# Revit family: Storage_Rack-Honeywell-Cabinet_Housing-584910(11)(13)
name_source: partatom
category: Furniture
revit_build: Autodesk Revit 2017 (Build: 20160225_1515(x64)
units: mm (PartAtom-declared; Revit-internal decimal feet)

## family parameters
Cut with Voids When Loaded = No
Host = Face
OmniClass Number = 23.40.20.27.17
OmniClass Title = Racking
Room Calculation Point = No
Shared = No

## types (3) — shared parameters
Finish = Metal - Honeywell - Stainless Steel - White
Manufacturer = Honeywell International
Manufacturer Fax Number = 02131/40615-606
Product Documentation Link = https://www.esser-systems.com
Product Page URL = https://www.esser-systems.com
URL = www.esser-systems.com
Version = 2017 - v1.0a
zero-valued in all types: Default Elevation

## per-type parameters (varying)
| type | C Door | Constraints | Depth | Description | Height | Model | Product Name | Upright | VARIODYN | Weight | Width |
| Cabinet 42 HU - 584911 | 139 mm  [stored 0.456037 ft] | 1 | 800 mm  [stored 2.62467 ft] | Upright cabinet without hinged frame 42 HU | 2100 mm  [stored 6.88976 ft] | 584911 | Upright Cabinet | Yes | No | 150.00 kgf | 800 mm  [stored 2.62467 ft] |
| Cabinet 26 HU - 584910 | 139 mm  [stored 0.456037 ft] | 2 | 800 mm  [stored 2.62467 ft] | Upright cabinet without hinged frame 42 HU | 1400 mm | 584910 | Upright Cabinet | Yes | No | 120.00 kgf | 800 mm  [stored 2.62467 ft] |
| Housing 19" - 584913 | 10 mm  [stored 0.0328084 ft] | 3 | 600 mm | 19“- housing for VARIODYN D1 Comprio | 610 mm | 584913 | Rack Housing | No | Yes | 29.00 kgf | 600 mm |

note: [stored X ft] marks values corroborated as IEEE doubles in the binary element streams (Revit-internal decimal feet)

## geometry (parser evidence)
native form markers: Sweep x2
no freeform markers — native parametric forms only
